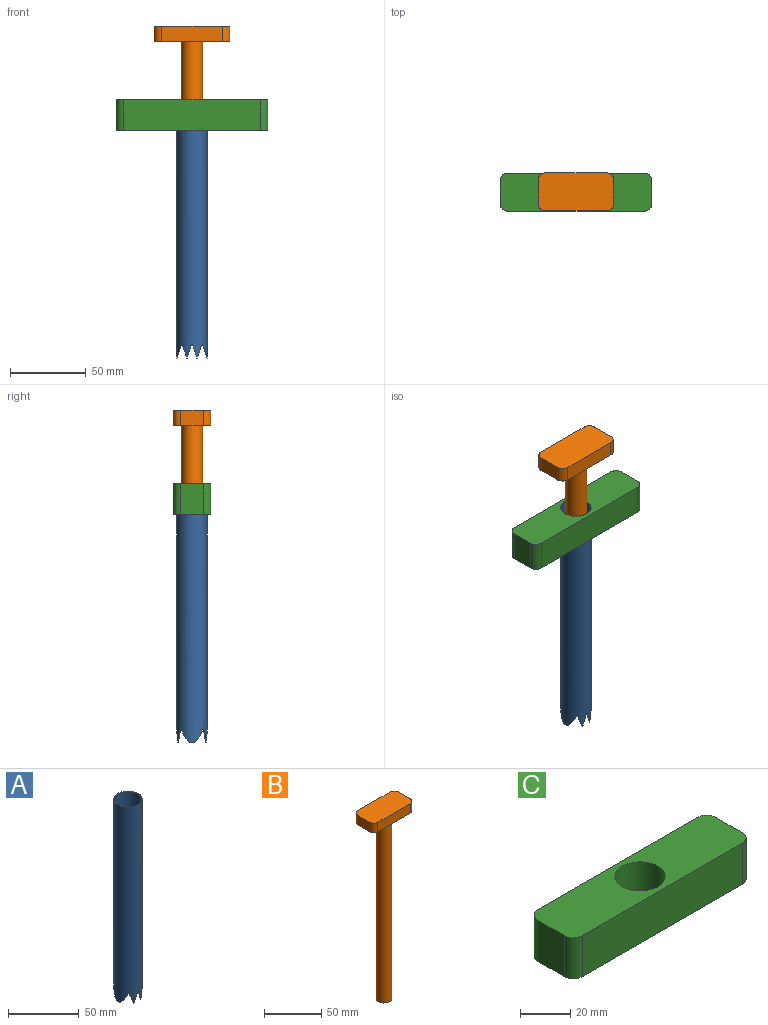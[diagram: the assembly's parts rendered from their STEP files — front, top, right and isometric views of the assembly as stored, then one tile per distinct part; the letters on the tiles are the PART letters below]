
ASSEMBLY  parts=3 mates=2
PART A: 19 faces, bbox 20x20x170 mm
  f0: cylinder r=10mm len=170mm, axis (0,0,-1), area 10436.5mm2, adj f1,f2,f4,f5,f6,f7,f8,f9
  f1: plane 0.61x0.21mm, normal (0,0,-1), area 0.1mm2, adj f0,f3,f10,f16
  f2: plane 0.61x0.21mm, normal (0,0,-1), area 0.1mm2, adj f0,f3,f11,f17
  f3: cylinder r=9.5mm len=170mm, axis (0,0,1), area 9882.8mm2, adj f1,f2,f4,f5,f8,f9,f10,f11
  f4: plane 0.61x0.21mm, normal (0,0,-1), area 0.1mm2, adj f0,f3,f12,f15
  f5: plane 0.61x0.21mm, normal (0,0,-1), area 0.1mm2, adj f0,f3,f13,f18
  f6: plane 2.82x0.1mm, normal (0,0,-1), area 0.2mm2, adj f0,f9
  f7: plane 2.82x0.1mm, normal (0,0,-1), area 0.2mm2, adj f0,f14
  f8: plane 20x20mm, normal (0,0,1), area 30.6mm2, adj f0,f3
  f9: plane 14.9x9.68mm, normal (-0.95,0,-0.32), area 24.6mm2, adj f0,f3,f6,f10,f11
  f10: plane 9.68x3.23mm, normal (0.95,0,-0.32), area 6.1mm2, adj f0,f1,f3,f9
  f11: plane 9.68x3.23mm, normal (0.95,0,-0.32), area 6.1mm2, adj f0,f2,f3,f9
  f12: plane 9.68x3.23mm, normal (-0.95,0,-0.32), area 6.1mm2, adj f0,f3,f4,f14
  f13: plane 9.68x3.23mm, normal (-0.95,0,-0.32), area 6.1mm2, adj f0,f3,f5,f14
  f14: plane 14.9x9.68mm, normal (0.95,0,-0.32), area 24.6mm2, adj f0,f3,f7,f12,f13
  f15: plane 9.68x3.23mm, normal (0.95,0,-0.32), area 5.2mm2, adj f0,f3,f4,f16
  f16: plane 9.68x3.23mm, normal (-0.95,0,-0.32), area 5.2mm2, adj f0,f1,f3,f15
  f17: plane 9.68x3.23mm, normal (-0.95,0,-0.32), area 5.2mm2, adj f0,f2,f3,f18
  f18: plane 9.68x3.23mm, normal (0.95,0,-0.32), area 5.2mm2, adj f0,f3,f5,f17
PART B: 12 faces, bbox 50x25x205 mm
  f0: plane 14x14mm, normal (0,0,-1), area 153.9mm2, adj f1
  f1: cylinder r=7mm len=195mm, axis (0,0,-1), area 8576.5mm2, adj f0,f2
  f2: plane 50x25mm, normal (0,0,-1), area 1074.6mm2, adj f1,f3,f5,f6,f7,f8,f9,f10
  f3: plane 15x10mm, normal (1,0,0), area 150mm2, adj f2,f4,f8,f11
  f4: plane 50x25mm, normal (0,0,1), area 1228.5mm2, adj f3,f5,f6,f7,f8,f9,f10,f11
  f5: plane 15x10mm, normal (-1,0,0), area 150mm2, adj f2,f4,f9,f10
  f6: plane 40x10mm, normal (0,1,0), area 400mm2, adj f2,f4,f8,f9
  f7: plane 40x10mm, normal (0,-1,0), area 400mm2, adj f2,f4,f10,f11
  f8: cylinder r=5mm len=10mm, axis (0,0,-1), area 78.5mm2, adj f2,f3,f4,f6
  f9: cylinder r=5mm len=10mm, axis (0,0,1), area 78.5mm2, adj f2,f4,f5,f6
  f10: cylinder r=5mm len=10mm, axis (0,0,-1), area 78.5mm2, adj f2,f4,f5,f7
  f11: cylinder r=5mm len=10mm, axis (0,0,1), area 78.5mm2, adj f2,f3,f4,f7
PART C: 11 faces, bbox 100x25x20 mm
  f0: plane 20x15mm, normal (1,0,0), area 300mm2, adj f5,f6,f8,f9
  f1: plane 90x20mm, normal (0,1,0), area 1800mm2, adj f5,f6,f9,f10
  f2: plane 20x15mm, normal (-1,0,0), area 300mm2, adj f5,f6,f7,f10
  f3: plane 90x20mm, normal (0,-1,0), area 1800mm2, adj f5,f6,f7,f8
  f4: cylinder r=10mm len=20mm, axis (0,0,-1), area 1256.6mm2, adj f5,f6
  f5: plane 100x25mm, normal (0,0,1), area 2164.4mm2, adj f0,f1,f2,f3,f4,f7,f8,f9
  f6: plane 100x25mm, normal (0,0,-1), area 2164.4mm2, adj f0,f1,f2,f3,f4,f7,f8,f9
  f7: cylinder r=5mm len=20mm, axis (0,0,1), area 157.1mm2, adj f2,f3,f5,f6
  f8: cylinder r=5mm len=20mm, axis (0,0,-1), area 157.1mm2, adj f0,f3,f5,f6
  f9: cylinder r=5mm len=20mm, axis (0,0,1), area 157.1mm2, adj f0,f1,f5,f6
  f10: cylinder r=5mm len=20mm, axis (0,0,-1), area 157.1mm2, adj f1,f2,f5,f6
PLACE A rot(axis=(0,0,-1),0deg) t=(2.2,-230.52,13.78)mm fixed
PLACE B t=(2.2,-230.52,95.96)mm
PLACE C rot(axis=(0,0,-1),0deg) t=(2.2,-230.52,78.78)mm
MATE slider B.f1 <-> C.f4  axis (0,0,-1) through (2.2,-230.52,-57.52)mm
MATE fastened A.f0 <-> C.f4  axis (0,0,1) through (2.2,-230.52,98.78)mm
